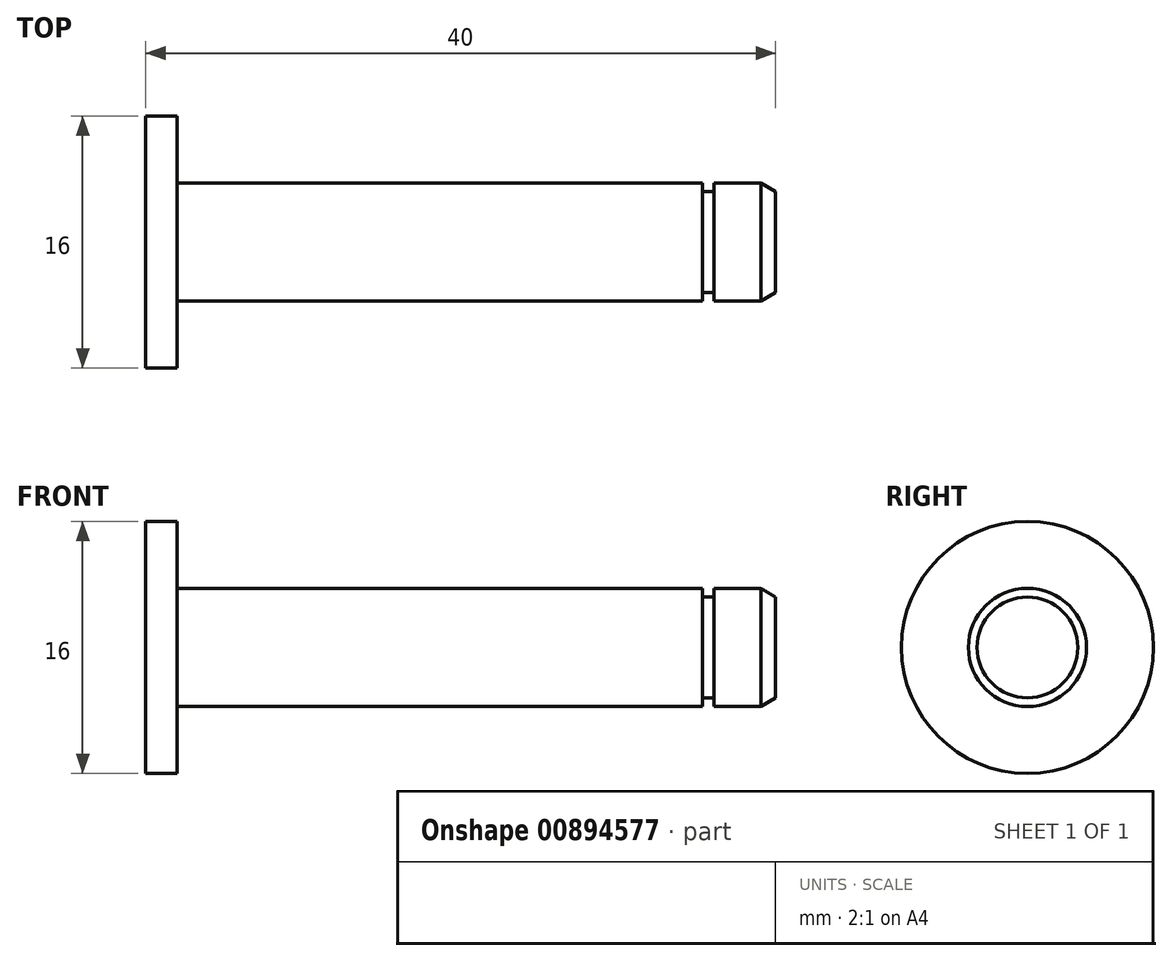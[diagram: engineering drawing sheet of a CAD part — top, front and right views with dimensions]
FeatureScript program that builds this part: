
annotation { "Feature Type Name" : "Feature", "Feature Type Description" : "" }
export const myFeature = defineFeature(function(context is Context, id is Id, definition is map)
    precondition{}
    {
        {
            var Q0;
            Q0=qCreatedBy(makeId("Front.planeOp"),FACE);
            var sketch = newSketch(context, id + "F0", { "sketchPlane" : qUnion([Q0])});
            skLineSegment(sketch, "E0", {"start": v(0, 0) * mm, "end": v(0, 8) * mm});
            skLineSegment(sketch, "E1", {"start": v(0, 8) * mm, "end": v(2, 8) * mm});
            skLineSegment(sketch, "E2", {"start": v(2, 8) * mm, "end": v(2, 3.75) * mm});
            skLineSegment(sketch, "E3", {"start": v(2, 3.75) * mm, "end": v(35.35, 3.75) * mm});
            skLineSegment(sketch, "E4", {"start": v(35.35, 3.75) * mm, "end": v(35.35, 3.2) * mm});
            skLineSegment(sketch, "E5", {"start": v(35.35, 3.2) * mm, "end": v(36.08, 3.2) * mm});
            skLineSegment(sketch, "E6", {"start": v(36.08, 3.2) * mm, "end": v(36.08, 3.75) * mm});
            skLineSegment(sketch, "E7", {"start": v(36.08, 3.75) * mm, "end": v(39.08, 3.75) * mm});
            skLineSegment(sketch, "E8", {"start": v(39.08, 3.75) * mm, "end": v(40, 3.2) * mm});
            skLineSegment(sketch, "E9", {"start": v(40, 3.2) * mm, "end": v(40, 0) * mm});
            skLineSegment(sketch, "E10", {"start": v(0, 0) * mm, "end": v(40, 0) * mm});
            skSolve(sketch);
        }
        {
            var Q0;
            Q0=makeQuery(id+"F0.imprint","IMPRINT",FACE,{"disambiguationData":[TD([[makeQuery(id+"F0.imprint","IMPRINT",EDGE,{"derivedFrom":sQuery(id+"F0.wireOp",EDGE,"E0")}),-1.0]])]});
            var Q1;
            Q1=sQuery(id+"F0.wireOp",EDGE,"E10");
            revolve(context, id + "F1", {"surfaceOperationType" : NewSurfaceOperationType.NEW, "entities" : qUnion([Q0]), "axis" : qUnion([Q1]), "revolveType" : RevolveType.FULL});
        }
    });
